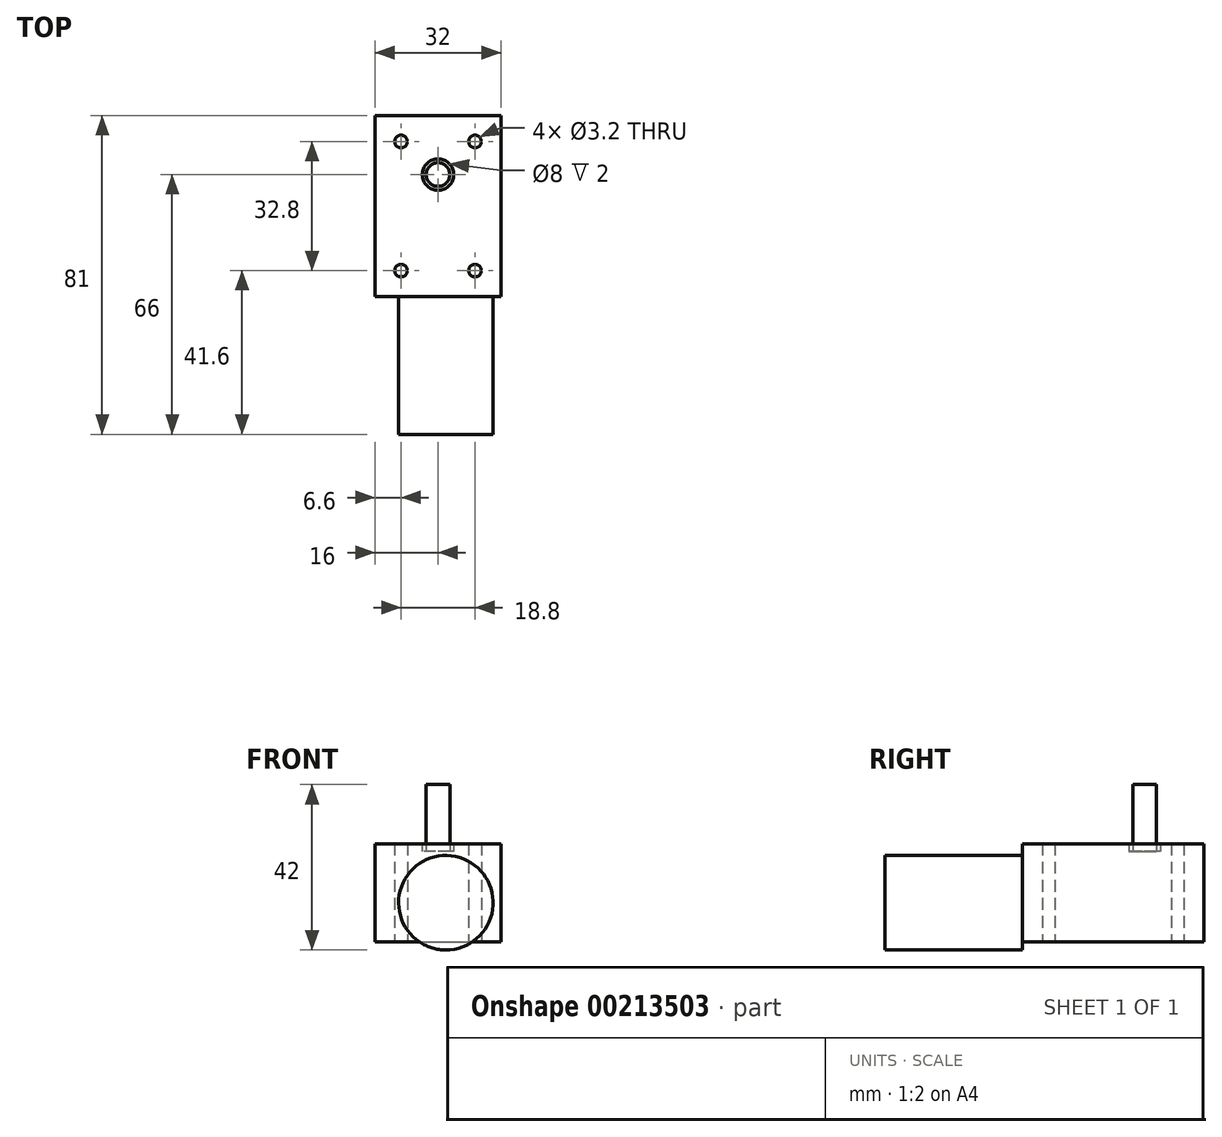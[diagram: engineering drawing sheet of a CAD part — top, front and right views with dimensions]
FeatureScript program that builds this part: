
annotation { "Feature Type Name" : "Feature", "Feature Type Description" : "" }
export const myFeature = defineFeature(function(context is Context, id is Id, definition is map)
    precondition{}
    {
        {
            var Q0;
            Q0=qCreatedBy(makeId("Top.planeOp"),FACE);
            var sketch = newSketch(context, id + "F0", { "sketchPlane" : qUnion([Q0])});
            skLineSegment(sketch, "E0.bottom", {"start": v(0, 0) * mm, "end": v(32, 0) * mm});
            skLineSegment(sketch, "E0.top", {"start": v(0, 46) * mm, "end": v(32, 46) * mm});
            skLineSegment(sketch, "E0.left", {"start": v(0, 0) * mm, "end": v(0, 46) * mm});
            skLineSegment(sketch, "E0.right", {"start": v(32, 0) * mm, "end": v(32, 46) * mm});
            skCircle(sketch, "E1", {"center": v(6.6, 6.6) * mm, "radius": 1.6 * mm});
            skCircle(sketch, "E2", {"center": v(6.6, 39.4) * mm, "radius": 1.6 * mm});
            skCircle(sketch, "E3", {"center": v(25.4, 6.6) * mm, "radius": 1.6 * mm});
            skCircle(sketch, "E4", {"center": v(25.4, 39.4) * mm, "radius": 1.6 * mm});
            skCircle(sketch, "E5", {"center": v(16, 31) * mm, "radius": 4 * mm});
            skPoint(sketch, "E5.centerSnap0", {"position": v(16, 46) * mm});
            skCircle(sketch, "E6", {"center": v(16, 31) * mm, "radius": 3 * mm});
            skSolve(sketch);
        }
        {
            var Q0;
            Q0=makeQuery(id+"F0.imprint","IMPRINT",FACE,{"disambiguationData":[TD([[makeQuery(id+"F0.imprint","IMPRINT",EDGE,{"derivedFrom":sQuery(id+"F0.wireOp",EDGE,"E0.bottom")}),1.0]])]});
            extrude(context, id + "F1", {"entities" : qUnion([Q0]), "depth" : 25 * mm});
        }
        {
            var Q0;
            Q0=makeQuery(id+"F1.opExtrude","SWEPT_FACE",FACE,{"disambiguationData":[OSD([sQuery(id+"F0.wireOp",EDGE,"E0.bottom")])]});
            var sketch = newSketch(context, id + "F2", { "sketchPlane" : qUnion([Q0])});
            skCircle(sketch, "E7", {"center": v(18, 10) * mm, "radius": 12 * mm});
            skSolve(sketch);
        }
        {
            var Q0;
            {var subQ0=sQuery(id+"F2.wireOp",EDGE,"E7");var subQ1=makeQuery(id+"F1.opExtrude","CAP_EDGE",EDGE,{"disambiguationData":[OSD([sQuery(id+"F0.wireOp",EDGE,"E0.bottom")])],"isStart":true});var subQ2=makeQuery(id+"F2.imprint","INTERSECT",VERTEX,{"disambiguationData":[OD(0.0)],"derivedFrom":[subQ1,subQ0]});Q0=makeQuery(id+"F2.imprint","IMPRINT",FACE,{"disambiguationData":[TD([[makeQuery(id+"F2.imprint","IMPRINT",EDGE,{"disambiguationData":[TD([[subQ2,-1.0]])],"derivedFrom":subQ0}),1.0]])]});}
            var Q1;
            {var subQ0=sQuery(id+"F2.wireOp",EDGE,"E7");var subQ1=makeQuery(id+"F1.opExtrude","CAP_EDGE",EDGE,{"disambiguationData":[OSD([sQuery(id+"F0.wireOp",EDGE,"E0.bottom")])],"isStart":true});var subQ2=makeQuery(id+"F2.imprint","INTERSECT",VERTEX,{"disambiguationData":[OD(0.0)],"derivedFrom":[subQ1,subQ0]});Q1=makeQuery(id+"F2.imprint","IMPRINT",FACE,{"disambiguationData":[TD([[makeQuery(id+"F2.imprint","IMPRINT",EDGE,{"disambiguationData":[TD([[subQ2,1.0]])],"derivedFrom":subQ0}),1.0]])]});}
            extrude(context, id + "F3", {"entities" : qUnion([Q0, Q1]), "operationType" : NewBodyOperationType.ADD, "depth" : 35 * mm});
        }
        {
            var Q0;
            Q0=makeQuery(id+"F0.imprint","IMPRINT",FACE,{"disambiguationData":[TD([[makeQuery(id+"F0.imprint","IMPRINT",EDGE,{"derivedFrom":sQuery(id+"F0.wireOp",EDGE,"E5")}),1.0]])]});
            extrude(context, id + "F4", {"entities" : qUnion([Q0]), "operationType" : NewBodyOperationType.ADD, "depth" : 23 * mm});
        }
        {
            var Q0;
            Q0=makeQuery(id+"F0.imprint","IMPRINT",FACE,{"disambiguationData":[TD([[makeQuery(id+"F0.imprint","IMPRINT",EDGE,{"derivedFrom":sQuery(id+"F0.wireOp",EDGE,"E6")}),1.0]])]});
            extrude(context, id + "F5", {"entities" : qUnion([Q0]), "operationType" : NewBodyOperationType.ADD, "depth" : 40 * mm});
        }
    });
